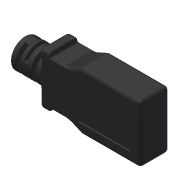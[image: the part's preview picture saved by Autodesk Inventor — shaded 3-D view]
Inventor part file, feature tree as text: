
AUTODESK INVENTOR PART (.ipt)
format: ipt  version: 2022 (Build 260153000, 153)  size: 471,552 bytes
history: native  units: in
note: dims shown in document units (in); Inventor stores cm internally (conversion verified against a paired STEP export)
features: sketch x7, extrude x6, fillet x5, mirror x4, plane x2, projected_geometry x2
ambient origin geometry x8: Origin, YZ Plane, XZ Plane, XY Plane, X Axis, Y Axis, Z Axis, Center Point
bodies: Solid1 (feature_tree)
feature tree (26):
  extrude  "Extrusion1"  Depth=0.62in
  extrude  "Extrusion2"  Depth=0.31in
  extrude  "Extrusion3"  Depth=0.18in
  mirror  "Mirror1"
  plane  "Work Plane1"
  mirror  "Mirror2"
  plane  "Work Plane2"
  extrude  "Extrusion4"  Depth=0.05in
  mirror  "Mirror3"
  extrude  "Extrusion5"  Depth=0.3in TaperAngle=0.0deg
  mirror  "Mirror4"
  extrude  "Extrusion6"  Depth=0.3in TaperAngle=0.0deg
  fillet  "Fillet1"  Radius=0.05in
  fillet  "Fillet2"  Radius=0.04in
  fillet  "Fillet3"  Radius=0.1in
  fillet  "Fillet4"  Radius=0.15in
  fillet  "Fillet5"  Radius=0.14in
  sketch  "Sketch7"  dims[d20=0.03in d21=0.1in d22=0.0in d23=0.1in d24=0.1in d25=0.4in d26=0.55in d27=0.015in d28=0.0in d29=0.08in d30=0.08in d31=0.24in d32=0.08in d33=0.015in d34=0.0in d35=0.035in d36=0.0125in d37=0.0125in d38=0.025in d39=0.005in]
  sketch  "Sketch1"  dims[d0=0.6in d1=0.62in]
  sketch  "Sketch2"  dims[d2=0.3in d3=0.31in]
  sketch  "Sketch3"  dims[d4=0.08in d5=0.18in]
  projected_geometry  "Projected Loop1"
  sketch  "Sketch4"  dims[d6=0.15in d7=0.05in]
  projected_geometry  "Projected Loop2"
  sketch  "Sketch5"  dims[d8=0.1in d9=0.3in d10=0.0in]
  sketch  "Sketch6"  dims[d11=0.15in d12=0.3in d13=0.0in d14=0.05in d15=0.04in d16=0.1in d17=0.0in d18=0.15in d19=0.14in]
